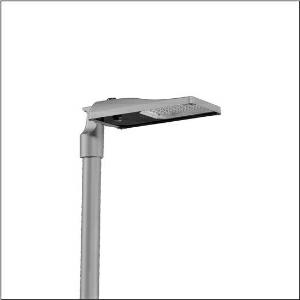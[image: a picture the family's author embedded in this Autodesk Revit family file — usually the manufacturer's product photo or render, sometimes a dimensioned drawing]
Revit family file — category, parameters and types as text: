
# Revit family: streetlight_sl_31_mini___p0_5a_5xh6v31t08ga_58c0
name_source: partatom
category: Lighting Fixtures
units: mm (PartAtom-declared; Revit-internal decimal feet)

## family parameters
Cut with Voids When Loaded = No
Host = Face
Light Source = No
Part Type = Normal
Room Calculation Point = No
Round Connector Dimension = Use Diameter
Shared = No

## types (1)
- --- (1 x LED, 5780 lm, 39.3 W, 3000K)
    Apparent Load = 39 VA
    CIE Flux Codes = 37 73 96 100 100
    Color Rendering = 70
    Color Temperature = 3000K
    Default Elevation = 1800 mm
    Description = Streetlight SL 31 mini D4i, Desk-Remote mast luminaire for post-top, side-entry; light control with lens of PMMA; light distribution: P0.5a, direct asymmetric distribution, for standard-compliant lighting for roads and squares; LED: luminous flux: 5.780lm, light colour: 730, colour temperature: 3000K; luminous efficacy: 147,1lm/W; control: pre-setting: logarithmic dimming characteristic, flexible luminous flux parameterisation, time-dependent luminous flux control, constant luminous flux control, power reduction, intelligent temperature release in ECG and LED module, overheat protection; luminaire housing, of diecast aluminium, Siteco® metallic grey (DB 702S), corrosivity category C5 high according to DIN EN ISO 12944; cover of toughened safety glass, transparent, opened without tools; mast flange of diecast aluminium, Siteco® metallic grey (DB 702S), spigot size: 76/60mm, mast flange included unmounted; with cable H07RN-F 2x 1.5mm², cable length: 6,5m, connection cable pre-assembled; mains connection: 220..240V, AC, 50/60Hz; power consumption (at start of service life): 39,3W / (at end of service life): 40,7W / (with reduced operation 50%): 18,1W; protection rating (complete): IP66; insulation class (complete): insulation class II (safety insulation); impact resistance: IK09; certification: CE, ENEC, ENEC+, VDE, UKCA, ZD4i; permissible operating ambient temperature for outdoor applications: -40..+50°C; packaging unit: 1 piece

Light Distribution: P0.5a
    Height = 76 mm
    Lamp = 1 x LED
    Lamp Light Flux = 5780 lm
    Lamp Power = 39.3 W
    Lamp count = 1
    Length = 547 mm
    Luminous efficacy = 147 lm/W
    Manufacturer = Siteco
    ModVariant = No
    Model = 5XH6V31T08GA
    Number of Poles = 1
    OnlyDefault = Yes
    Power Factor = 1
    Product Name = Streetlight SL 31 mini | P0.5a
    Product group = mast luminaire | pylon top
    ProductGroupID = 6100
    Protection Class = Protection class II
    Protection Degree = IP 66
    RLX_Detail_Level = 1
    RLX_Emergency_Light_Flux = 0 lm
    RLX_Emergency_Type = 0
    RLX_Emergency_Type_DB = No
    RlxData = <blob elided: 39417 chars, md5=f4f2ae2f>
    Socket = socket
    Standby Power = 0 W
    System Light Flux = 5780 lm
    System Power = 39 W
    Type Comments = factory setting: luminous flux: 100 % | dim-lin: 254 | 798 mA
    Type Image = l_1300332.jpg
    URL = http://relux.com
    VarID = @adj_058598
    Voltage = 0 V
    Weight = 0.00 kg
    Width = 265 mm

## geometry (parser evidence)
native form markers: Blend x4, Sweep x9
no freeform markers — native parametric forms only
